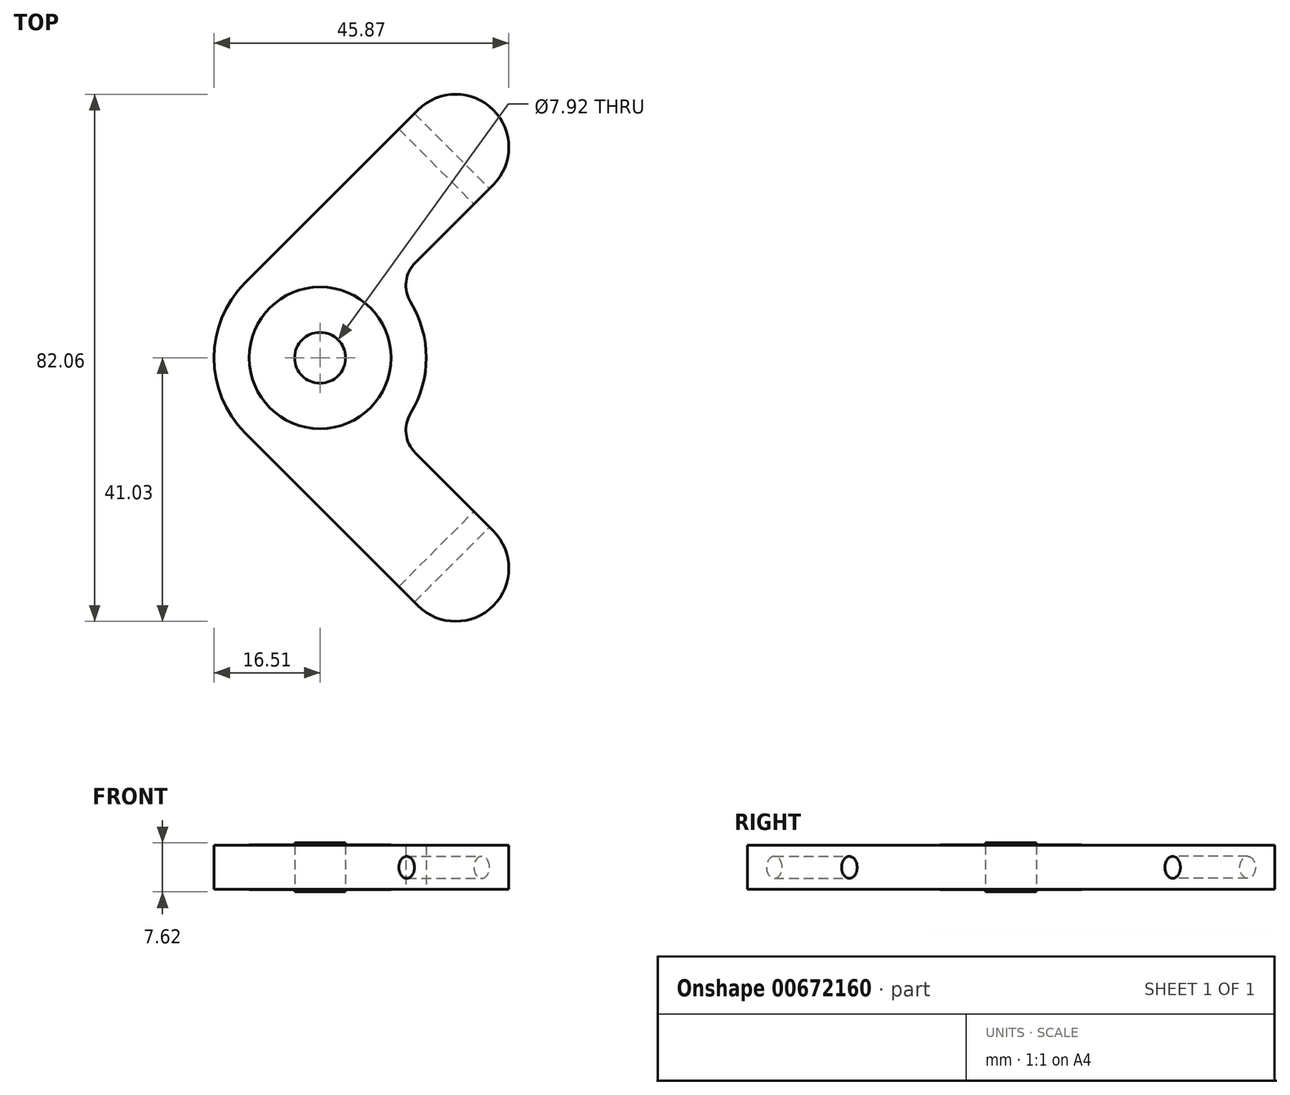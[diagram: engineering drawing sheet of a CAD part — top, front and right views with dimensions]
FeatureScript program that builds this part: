
annotation { "Feature Type Name" : "Feature", "Feature Type Description" : "" }
export const myFeature = defineFeature(function(context is Context, id is Id, definition is map)
    precondition{}
    {
        {
            var Q0;
            Q0=qCreatedBy(makeId("Top.planeOp"),FACE);
            var sketch = newSketch(context, id + "F0", { "sketchPlane" : qUnion([Q0])});
            skCircle(sketch, "E0", {"center": v(0, 0) * mm, "radius": 3.96 * mm});
            skCircle(sketch, "E1", {"center": v(0, 0) * mm, "radius": 11.02 * mm});
            skSolve(sketch);
        }
        {
            var Q0;
            Q0 = qSketchRegion(id + "F0", true);
            var Q1;
            Q1 = qConstructionFilter(qBodyType(qCreatedBy(id + "F0" ,EDGE), BodyType.WIRE), ConstructionObject.NO);
            extrude(context, id + "F1", {"entities" : qUnion([Q0]), "surfaceEntities" : qUnion([Q1]), "endBound" : BoundingType.SYMMETRIC, "depth" : 7 * mm, "offsetDistance" : 25.4 * mm});
        }
        {
            var Q0;
            Q0=qCreatedBy(makeId("Top.planeOp"),FACE);
            var sketch = newSketch(context, id + "F2", { "sketchPlane" : qUnion([Q0])});
            skCircle(sketch, "E2", {"center": v(0, 0) * mm, "radius": 11.02 * mm});
            skArc(sketch, "E3", {"start": v(-11.67, 11.67) * mm, "mid": v(0, -16.51) * mm, "end": v(11.67, 11.67) * mm});
            skLineSegment(sketch, "E4", {"start": v(-11.67, 11.67) * mm, "end": v(15.27, 38.62) * mm});
            skLineSegment(sketch, "E5", {"start": v(26.94, 26.94) * mm, "end": v(11.67, 11.67) * mm});
            skArc(sketch, "E6", {"start": v(26.94, 26.94) * mm, "mid": v(26.94, 38.62) * mm, "end": v(15.27, 38.62) * mm});
            skLineSegment(sketch, "E7", {"start": v(11.67, 11.67) * mm, "end": v(0, 0) * mm, "construction": true});
            skSolve(sketch);
        }
        {
            var Q0;
            Q0 = qSketchRegion(id + "F2", true);
            var Q1;
            Q1=makeQuery(id+"F1.opExtrude","CAP_FACE",FACE,{"disambiguationData":[OSD([sQuery(id+"F0.wireOp",EDGE,"E0"),sQuery(id+"F0.wireOp",EDGE,"E1")])],"isStart":false});
            extrude(context, id + "F3", {"entities" : qUnion([Q0]), "endBound" : BoundingType.SYMMETRIC, "depth" : 6.86 * mm, "endBoundEntityFace" : qUnion([Q1]), "offsetDistance" : 25.4 * mm});
        }
        {
            var Q0;
            Q0=makeQuery(id+"F3.opExtrude","SWEPT_EDGE",EDGE,{"disambiguationData":[OSD([sQuery(id+"F2.wireOp",EDGE,"E3"),sQuery(id+"F2.wireOp",EDGE,"E5")])]});
            fillet(context, id + "F4", {"entities" : qUnion([Q0]), "radius" : 5.08 * mm, "tangentPropagation" : true, "allowEdgeOverflow" : false});
        }
        {
            var Q0;
            Q0=makeQuery(id+"F3.opExtrude","SWEPT_FACE",FACE,{"disambiguationData":[OSD([sQuery(id+"F2.wireOp",EDGE,"E5")])]});
            var sketch = newSketch(context, id + "F5", { "sketchPlane" : qUnion([Q0])});
            skCircle(sketch, "E8", {"center": v(35.56, 0) * mm, "radius": 1.71 * mm});
            skPoint(sketch, "E9", {"position": v(38.1, 0) * mm});
            skSolve(sketch);
        }
        {
            var Q0;
            Q0 = qSketchRegion(id + "F5", true);
            extrude(context, id + "F6", {"entities" : qUnion([Q0]), "operationType" : NewBodyOperationType.REMOVE, "endBound" : BoundingType.THROUGH_ALL, "oppositeDirection" : true, "depth" : 25.4 * mm, "offsetDistance" : 25.4 * mm});
        }
        {
            var Q0;
            Q0=makeQuery(id+"F3.opExtrude","SWEPT_BODY",BODY,{"disambiguationData":[OSD([sQuery(id+"F2.wireOp",EDGE,"E2"),sQuery(id+"F2.wireOp",EDGE,"E3"),sQuery(id+"F2.wireOp",EDGE,"E4"),sQuery(id+"F2.wireOp",EDGE,"E5"),sQuery(id+"F2.wireOp",EDGE,"E6")])]});
            var Q1;
            Q1=qCreatedBy(makeId("Front.planeOp"),FACE);
            mirror(context, id + "F7", {"operationType" : NewBodyOperationType.ADD, "entities" : qUnion([Q0]), "mirrorPlane" : qUnion([Q1])});
        }
        {
            var Q0;
            Q0=qCreatedBy(makeId("Top.planeOp"),FACE);
            var sketch = newSketch(context, id + "F8", { "sketchPlane" : qUnion([Q0])});
            skCircle(sketch, "E10", {"center": v(0, 0) * mm, "radius": 3.96 * mm});
            skSolve(sketch);
        }
        {
            var Q0;
            Q0 = qSketchRegion(id + "F8", true);
            extrude(context, id + "F9", {"entities" : qUnion([Q0]), "endBound" : BoundingType.SYMMETRIC, "depth" : 7.62 * mm, "offsetDistance" : 25.4 * mm});
        }
    });
